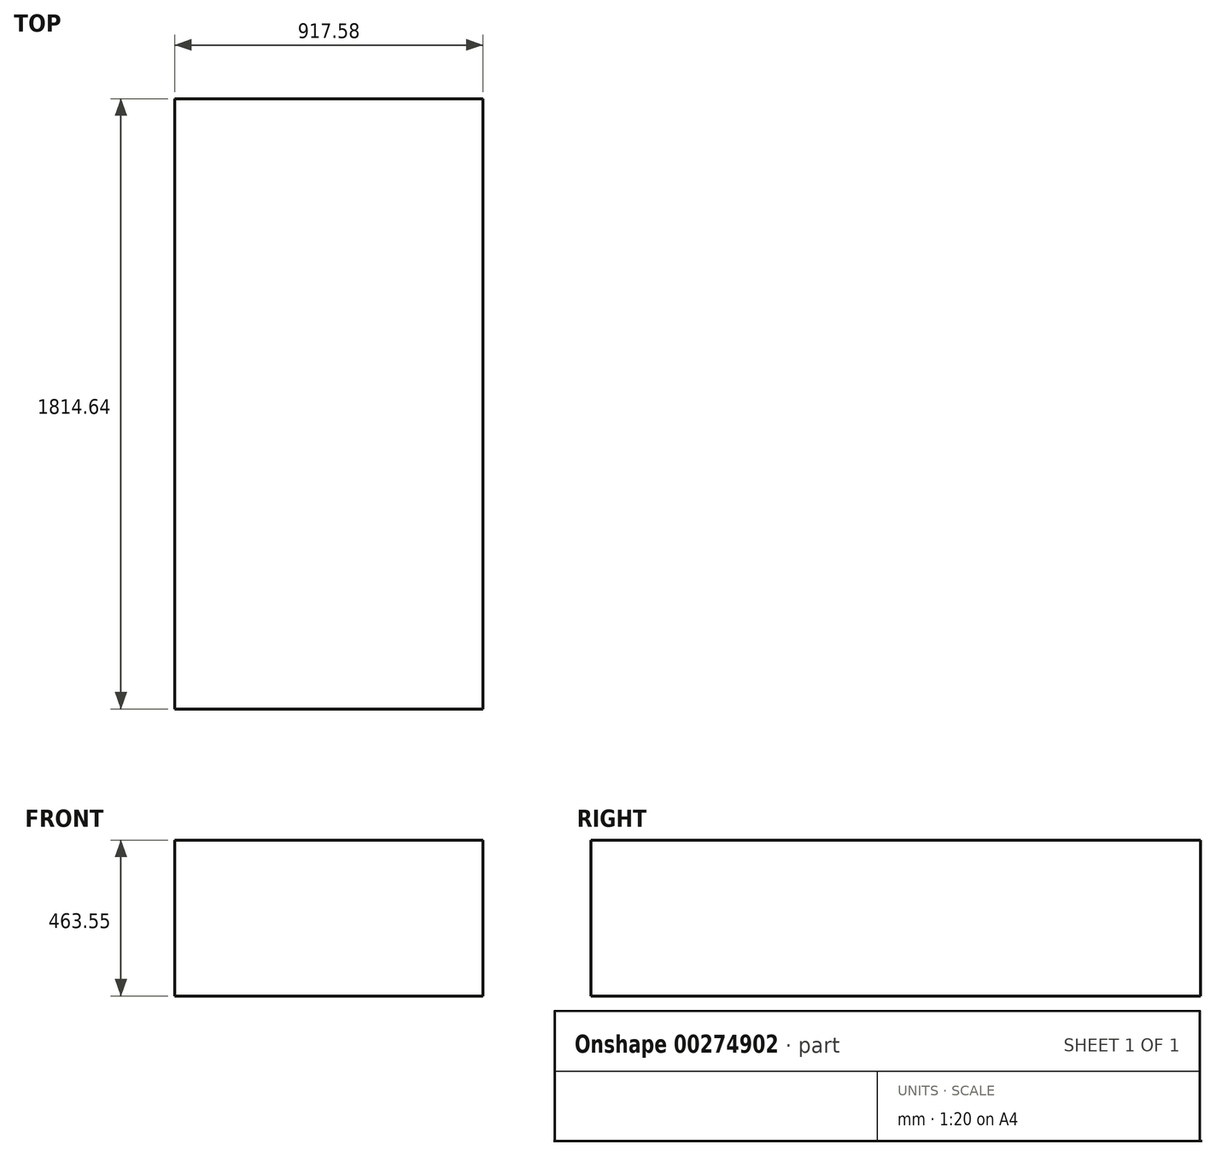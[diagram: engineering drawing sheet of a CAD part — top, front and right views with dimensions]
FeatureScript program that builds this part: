
annotation { "Feature Type Name" : "Feature", "Feature Type Description" : "" }
export const myFeature = defineFeature(function(context is Context, id is Id, definition is map)
    precondition{}
    {
        {
            var Q0;
            Q0=qCreatedBy(makeId("Top.planeOp"),FACE);
            var sketch = newSketch(context, id + "F0", { "sketchPlane" : qUnion([Q0])});
            skLineSegment(sketch, "E0.bottom", {"start": v(0, 0) * mm, "end": v(917.58, 0) * mm});
            skLineSegment(sketch, "E0.top", {"start": v(0, 1498.6) * mm, "end": v(917.57, 1498.6) * mm});
            skLineSegment(sketch, "E0.left", {"start": v(0, 0) * mm, "end": v(0, 1498.6) * mm});
            skLineSegment(sketch, "E0.right", {"start": v(917.58, 0) * mm, "end": v(917.57, 1498.6) * mm});
            skSolve(sketch);
        }
        {
            var Q0;
            Q0=makeQuery(id+"F0.imprint","IMPRINT",FACE,{"disambiguationData":[TD([[makeQuery(id+"F0.imprint","IMPRINT",EDGE,{"derivedFrom":sQuery(id+"F0.wireOp",EDGE,"E0.bottom")}),1.0]])]});
            extrude(context, id + "F1", {"entities" : qUnion([Q0]), "depth" : 463.55 * mm});
        }
        {
            var Q0;
            Q0=makeQuery(id+"F1.opExtrude","SWEPT_FACE",FACE,{"disambiguationData":[OSD([sQuery(id+"F0.wireOp",EDGE,"E0.bottom")])]});
            extrude(context, id + "F2", {"entities" : qUnion([Q0]), "operationType" : NewBodyOperationType.ADD, "depth" : 474.98 * mm});
        }
        {
            var Q0;
            Q0=makeQuery(id+"F2.opExtrude","CAP_FACE",FACE,{"disambiguationData":[OSD([sQuery(id+"F0.wireOp",EDGE,"E0.bottom")])],"isStart":false});
            extrude(context, id + "F3", {"entities" : qUnion([Q0]), "operationType" : NewBodyOperationType.REMOVE, "oppositeDirection" : true, "depth" : 158.94 * mm});
        }
    });
